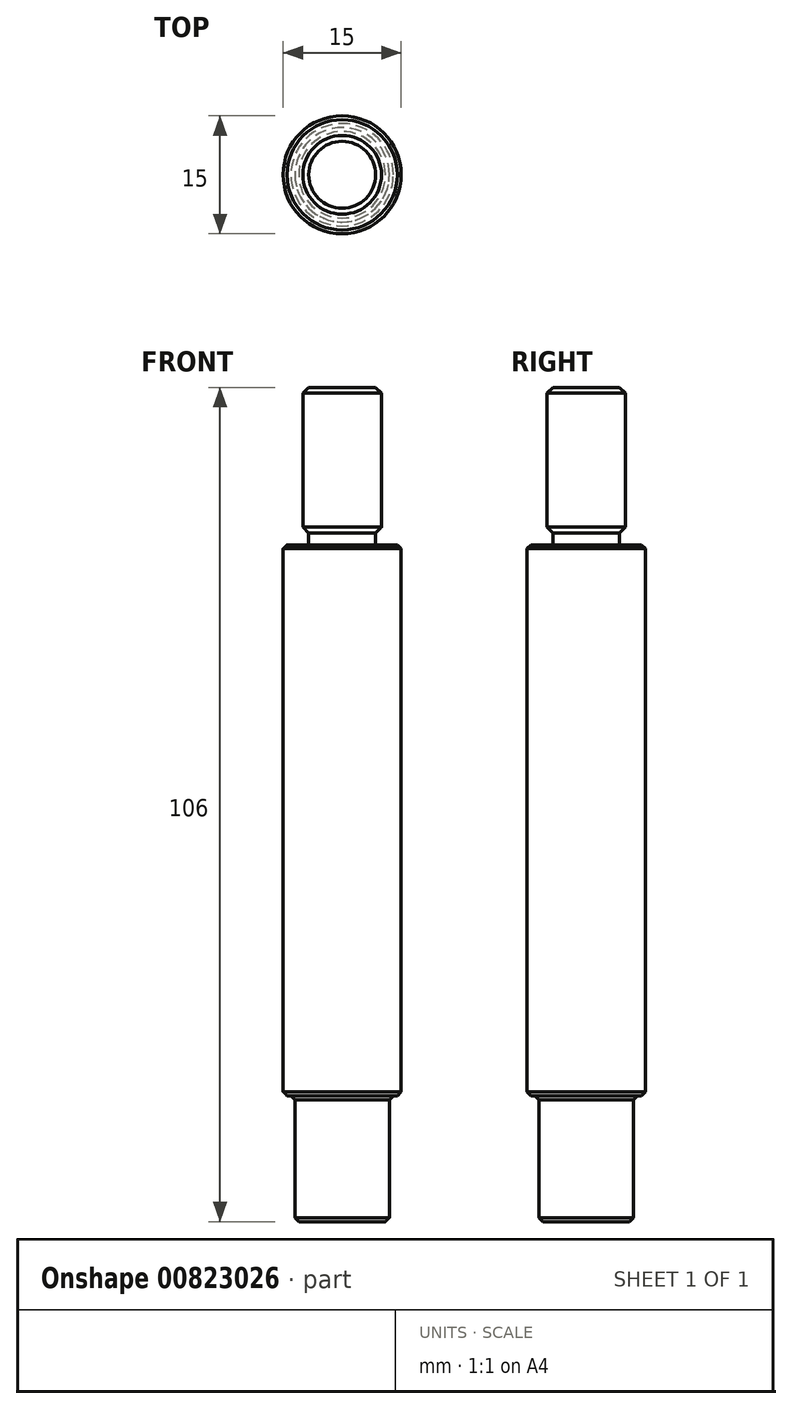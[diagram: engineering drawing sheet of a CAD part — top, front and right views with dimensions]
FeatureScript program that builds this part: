
annotation { "Feature Type Name" : "Feature", "Feature Type Description" : "" }
export const myFeature = defineFeature(function(context is Context, id is Id, definition is map)
    precondition{}
    {
        {
            var Q0;
            Q0=qCreatedBy(makeId("Front.planeOp"),FACE);
            var sketch = newSketch(context, id + "F0", { "sketchPlane" : qUnion([Q0])});
            skLineSegment(sketch, "E0", {"start": v(0, 0) * mm, "end": v(-6, 0) * mm});
            skLineSegment(sketch, "E1", {"start": v(-6, 0) * mm, "end": v(-6, 14.25) * mm});
            skLineSegment(sketch, "E2", {"start": v(-7.5, 16) * mm, "end": v(-6, 16) * mm});
            skLineSegment(sketch, "E3", {"start": v(-7.5, 16) * mm, "end": v(-7.5, 86) * mm});
            skLineSegment(sketch, "E4", {"start": v(-5, 86) * mm, "end": v(-7.5, 86) * mm});
            skLineSegment(sketch, "E5", {"start": v(-5, 87.5) * mm, "end": v(-5, 106) * mm});
            skLineSegment(sketch, "E6", {"start": v(-5, 106) * mm, "end": v(0, 106) * mm});
            skLineSegment(sketch, "E7", {"start": v(0, 106) * mm, "end": v(0, 0) * mm});
            skLineSegment(sketch, "E8", {"start": v(0, 0) * mm, "end": v(0, -4.4) * mm, "construction": true});
            skLineSegment(sketch, "E9", {"start": v(-6, 16) * mm, "end": v(-5.15, 16) * mm, "construction": true});
            skLineSegment(sketch, "E10", {"start": v(-5.15, 16) * mm, "end": v(-5.15, 14.25) * mm, "construction": true});
            skLineSegment(sketch, "E11", {"start": v(-5.15, 14.25) * mm, "end": v(-6, 14.25) * mm, "construction": true});
            skLineSegment(sketch, "E12", {"start": v(-5, 86) * mm, "end": v(-4.25, 86) * mm});
            skLineSegment(sketch, "E13", {"start": v(-4.25, 86) * mm, "end": v(-4.25, 87.5) * mm});
            skLineSegment(sketch, "E14", {"start": v(-4.25, 87.5) * mm, "end": v(-5, 87.5) * mm});
            skLineSegment(sketch, "E15", {"start": v(-6, 16) * mm, "end": v(-6, 14.25) * mm});
            skSolve(sketch);
        }
        {
            var Q0;
            Q0=makeQuery(id+"F0.imprint","IMPRINT",FACE,{"disambiguationData":[TD([[makeQuery(id+"F0.imprint","IMPRINT",EDGE,{"derivedFrom":sQuery(id+"F0.wireOp",EDGE,"E0")}),-1.0]])]});
            var Q1;
            Q1=sQuery(id+"F0.wireOp",EDGE,"E7");
            revolve(context, id + "F1", {"surfaceOperationType" : NewSurfaceOperationType.NEW, "entities" : qUnion([Q0]), "axis" : qUnion([Q1]), "revolveType" : RevolveType.FULL});
        }
        {
            var Q0;
            Q0=makeQuery(id+"F1.opRevolve","SWEPT_FACE",FACE,{"disambiguationData":[OSD([sQuery(id+"F0.wireOp",EDGE,"E5")])]});
            chamfer(context, id + "F2", {"entities" : qUnion([Q0]), "width" : 0.75 * mm, "tangentPropagation" : true});
        }
        {
            var Q0;
            Q0=makeQuery(id+"F1.opRevolve","SWEPT_FACE",FACE,{"disambiguationData":[OSD([sQuery(id+"F0.wireOp",EDGE,"E3")])]});
            var Q1;
            Q1=makeQuery(id+"F1.opRevolve","SWEPT_EDGE",EDGE,{"disambiguationData":[OSD([sQuery(id+"F0.wireOp",EDGE,"E0"),sQuery(id+"F0.wireOp",EDGE,"E1")])]});
            var Q2;
            Q2=makeQuery(id+"F1.opRevolve","SWEPT_EDGE",EDGE,{"disambiguationData":[OSD([sQuery(id+"F0.wireOp",EDGE,"E2"),sQuery(id+"F0.wireOp",EDGE,"E15")])]});
            chamfer(context, id + "F3", {"entities" : qUnion([Q0, Q1, Q2]), "width" : 0.5 * mm, "tangentPropagation" : true});
        }
    });
